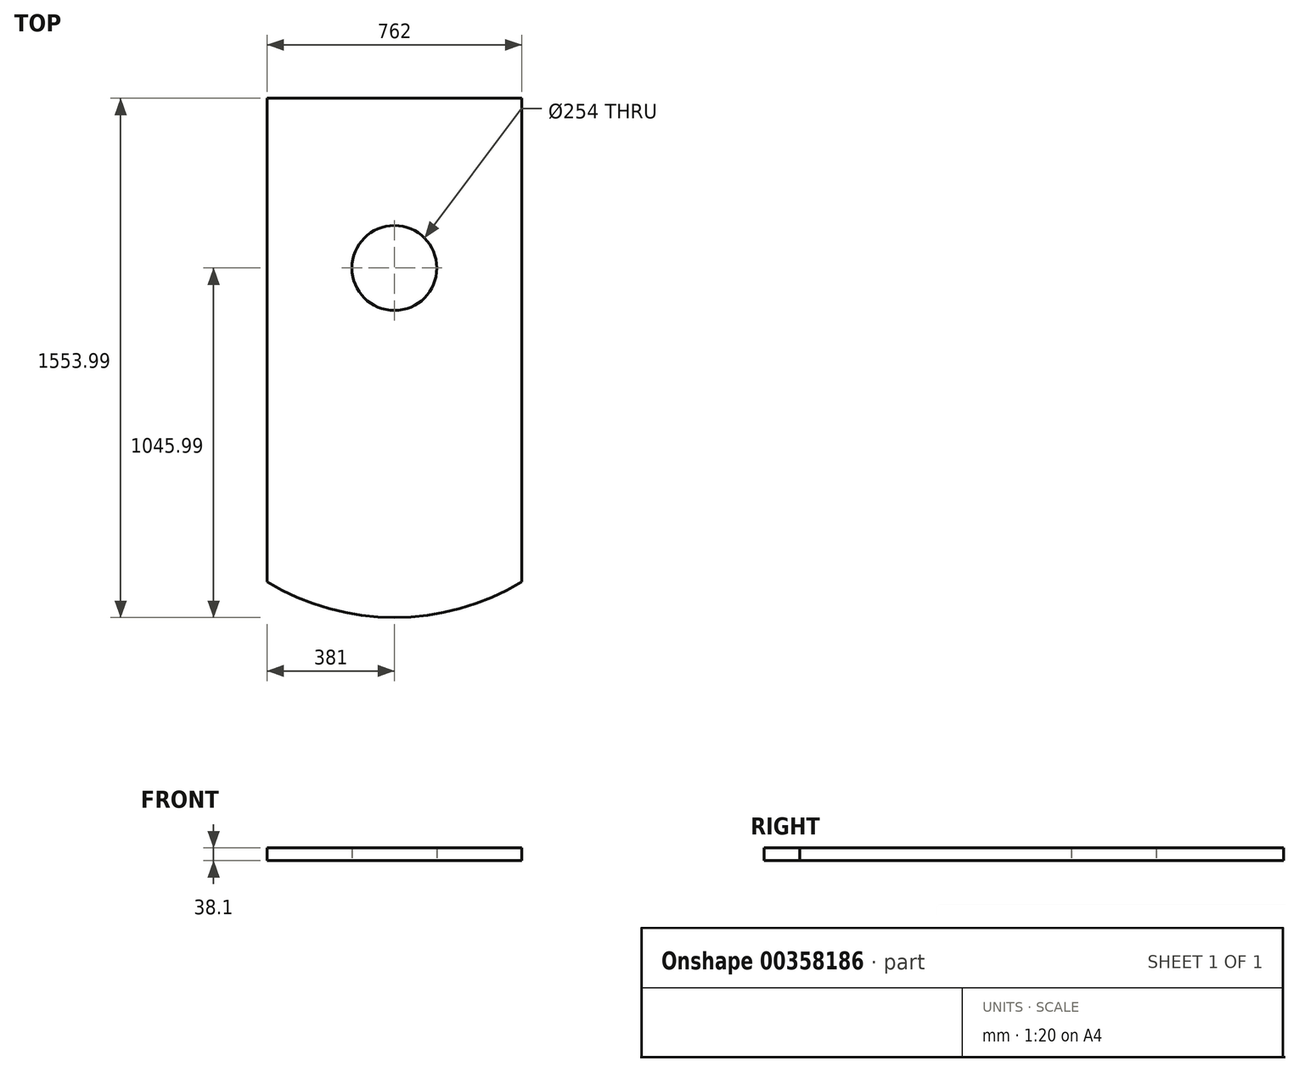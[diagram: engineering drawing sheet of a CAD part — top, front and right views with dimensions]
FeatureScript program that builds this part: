
annotation { "Feature Type Name" : "Feature", "Feature Type Description" : "" }
export const myFeature = defineFeature(function(context is Context, id is Id, definition is map)
    precondition{}
    {
        {
            var Q0;
            Q0=qCreatedBy(makeId("Top.planeOp"),FACE);
            var sketch = newSketch(context, id + "F0", { "sketchPlane" : qUnion([Q0])});
            skLineSegment(sketch, "E0.top", {"start": v(381, 723.9) * mm, "end": v(-381, 723.9) * mm});
            skLineSegment(sketch, "E0.left", {"start": v(381, -723.9) * mm, "end": v(381, 723.9) * mm});
            skLineSegment(sketch, "E0.right", {"start": v(-381, -723.9) * mm, "end": v(-381, 723.9) * mm});
            skPoint(sketch, "E0.middle", {"position": v(0, 0) * mm});
            skArc(sketch, "E1", {"start": v(-381, -723.9) * mm, "mid": v(0, -830.09) * mm, "end": v(381, -723.9) * mm});
            skCircle(sketch, "E2", {"center": v(0, 215.9) * mm, "radius": 127 * mm});
            skPoint(sketch, "E2.centerSnap0", {"position": v(0, 723.9) * mm});
            skSolve(sketch);
        }
        {
            var Q0;
            Q0 = qSketchRegion(id + "F0", true);
            extrude(context, id + "F1", {"entities" : qUnion([Q0]), "depth" : 38.1 * mm});
        }
    });
